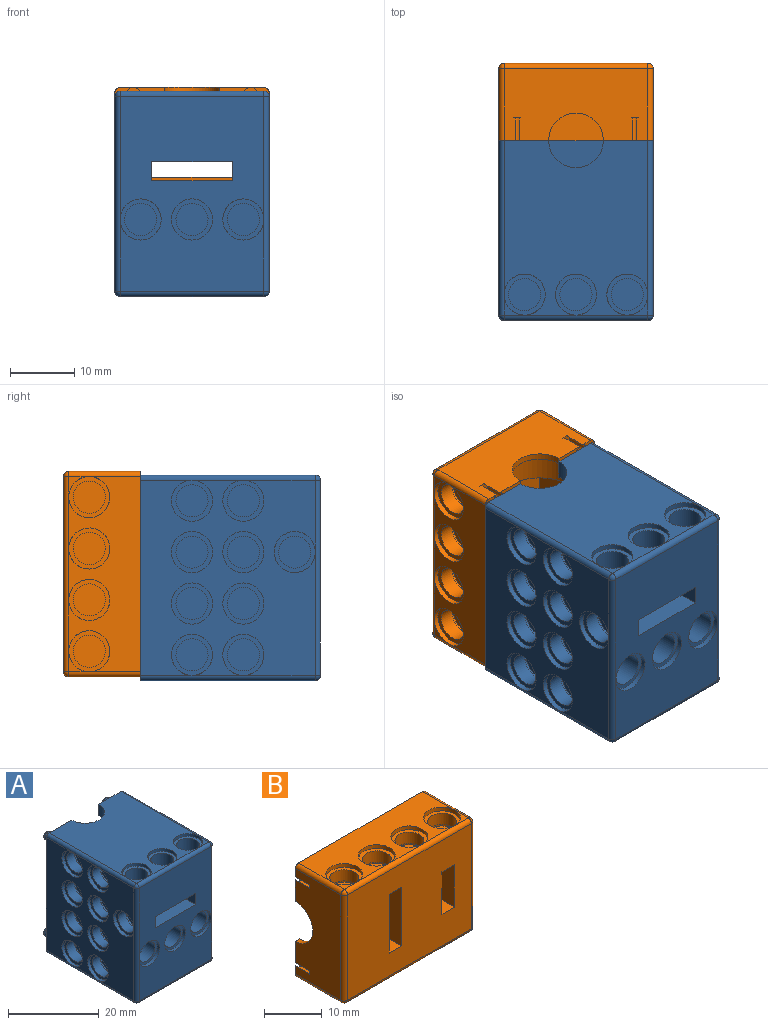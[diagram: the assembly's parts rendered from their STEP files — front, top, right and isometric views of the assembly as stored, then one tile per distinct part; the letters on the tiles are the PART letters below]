
ASSEMBLY  parts=2 mates=1
PART A: 209 faces, bbox 24x31x32 mm
  f0: plane 27.2x22.4mm, normal (0,0,-1), area 508.4mm2, adj f13,f167,f169,f171,f185,f189,f190
  f1: plane 3.2x3.2mm, normal (0,0,-1), area 2.2mm2, adj f171,f189,f190
  f2: plane 27.2x22.4mm, normal (0,0,1), area 480mm2, adj f13,f22,f149,f151,f153,f187,f193,f196
  f3: plane 3.2x3.2mm, normal (0,0,1), area 2.2mm2, adj f149,f193,f196
  f4: plane 3.2x3.2mm, normal (0,0,1), area 2.2mm2, adj f153,f187,f193
  f5: plane 30.4x27.2mm, normal (-1,0,0), area 537.4mm2, adj f13,f23,f25,f27,f29,f31,f33,f35
  f6: plane 3.2x3.2mm, normal (0,0,-1), area 2.2mm2, adj f167,f185,f189
  f7: plane 28x22mm, normal (1,0,0), area 407mm2, adj f8,f10,f12,f13,f14,f15,f16,f17
  f8: plane 12.5x11mm, normal (0,0,-1), area 137.5mm2, adj f7,f9,f12,f15
  f9: plane 28x22mm, normal (-1,0,0), area 407mm2, adj f8,f10,f12,f13,f14,f15,f16,f17
  f10: plane 12.5x11mm, normal (0,0,1), area 137.5mm2, adj f7,f9,f12,f16
  f11: plane 30.4x27.2mm, normal (1,0,0), area 537.4mm2, adj f13,f77,f79,f81,f83,f85,f87,f89
  f12: plane 30.4x22.4mm, normal (0,-1,0), area 547mm2, adj f7,f8,f9,f10,f131,f133,f135,f188
  f13: plane 32x24mm, normal (0,1,0), area 404.4mm2, adj f0,f2,f5,f7,f9,f11,f17,f19
  f14: plane 17x12.5mm, normal (0,0,-1), area 139.5mm2, adj f7,f9,f15,f18,f19,f20
  f15: plane 12.5x4mm, normal (0,1,0), area 50mm2, adj f7,f8,f9,f14
  f16: plane 15x12.5mm, normal (0,1,0), area 187.5mm2, adj f7,f9,f10,f17
  f17: plane 17x12.5mm, normal (0,0,1), area 212.5mm2, adj f7,f9,f13,f16
  f18: cylinder r=2.75mm len=5.5mm, axis (0,0,1), area 37.6mm2, adj f14,f19,f20,f21
  f19: cylinder r=6.25mm len=5.63mm, axis (0,0,1), area 28mm2, adj f13,f14,f18,f21
  f20: cylinder r=6.25mm len=5.63mm, axis (0,0,1), area 28mm2, adj f13,f14,f18,f21
  f21: plane 12.5x8.75mm, normal (0,0,-1), area 44.6mm2, adj f13,f18,f19,f20,f22
  f22: cylinder r=4.25mm len=8.5mm, axis (0,0,1), area 40.1mm2, adj f2,f13,f21
  f23: cylinder r=3.2mm len=6.4mm, axis (-1,0,0), area 16.1mm2, adj f5,f24
  f24: plane 6.4x6.4mm, normal (-1,0,0), area 12.5mm2, adj f23,f44
  f25: cylinder r=3.2mm len=6.4mm, axis (-1,0,0), area 16.1mm2, adj f5,f26
  f26: plane 6.4x6.4mm, normal (-1,0,0), area 12.5mm2, adj f25,f48
  f27: cylinder r=3.2mm len=6.4mm, axis (-1,0,0), area 16.1mm2, adj f5,f28
  f28: plane 6.4x6.4mm, normal (-1,0,0), area 12.5mm2, adj f27,f52
  f29: cylinder r=3.2mm len=6.4mm, axis (-1,0,0), area 16.1mm2, adj f5,f30
  f30: plane 6.4x6.4mm, normal (-1,0,0), area 12.5mm2, adj f29,f56
  f31: cylinder r=3.2mm len=6.4mm, axis (-1,0,0), area 16.1mm2, adj f5,f32
  f32: plane 6.4x6.4mm, normal (-1,0,0), area 12.5mm2, adj f31,f60
  f33: cylinder r=3.2mm len=6.4mm, axis (-1,0,0), area 16.1mm2, adj f5,f34
  f34: plane 6.4x6.4mm, normal (-1,0,0), area 12.5mm2, adj f33,f64
  f35: cylinder r=3.2mm len=6.4mm, axis (-1,0,0), area 16.1mm2, adj f5,f36
  f36: plane 6.4x6.4mm, normal (-1,0,0), area 12.5mm2, adj f35,f68
  f37: cylinder r=3.2mm len=6.4mm, axis (-1,0,0), area 16.1mm2, adj f5,f38
  f38: plane 6.4x6.4mm, normal (-1,0,0), area 12.5mm2, adj f37,f72
  f39: cylinder r=3.2mm len=6.4mm, axis (-1,0,0), area 16.1mm2, adj f5,f40
  f40: plane 6.4x6.4mm, normal (-1,0,0), area 12.5mm2, adj f39,f76
  f41: plane 6.4x6.4mm, normal (-1,0,0), area 32.2mm2, adj f42
  f42: cylinder r=3.2mm len=6.4mm, axis (-1,0,0), area 16.1mm2, adj f41,f43
  f43: plane 6.4x6.4mm, normal (1,0,0), area 12.5mm2, adj f42,f44
  f44: cylinder r=2.5mm len=5mm, axis (-1,0,0), area 37.7mm2, adj f24,f43
  f45: plane 6.4x6.4mm, normal (-1,0,0), area 32.2mm2, adj f46
  f46: cylinder r=3.2mm len=6.4mm, axis (-1,0,0), area 16.1mm2, adj f45,f47
  f47: plane 6.4x6.4mm, normal (1,0,0), area 12.5mm2, adj f46,f48
  f48: cylinder r=2.5mm len=5mm, axis (-1,0,0), area 37.7mm2, adj f26,f47
  f49: plane 6.4x6.4mm, normal (-1,0,0), area 32.2mm2, adj f50
  f50: cylinder r=3.2mm len=6.4mm, axis (-1,0,0), area 16.1mm2, adj f49,f51
  f51: plane 6.4x6.4mm, normal (1,0,0), area 12.5mm2, adj f50,f52
  f52: cylinder r=2.5mm len=5mm, axis (-1,0,0), area 37.7mm2, adj f28,f51
  f53: plane 6.4x6.4mm, normal (-1,0,0), area 32.2mm2, adj f54
  f54: cylinder r=3.2mm len=6.4mm, axis (-1,0,0), area 16.1mm2, adj f53,f55
  f55: plane 6.4x6.4mm, normal (1,0,0), area 12.5mm2, adj f54,f56
  f56: cylinder r=2.5mm len=5mm, axis (-1,0,0), area 37.7mm2, adj f30,f55
  f57: plane 6.4x6.4mm, normal (-1,0,0), area 32.2mm2, adj f58
  f58: cylinder r=3.2mm len=6.4mm, axis (-1,0,0), area 16.1mm2, adj f57,f59
  f59: plane 6.4x6.4mm, normal (1,0,0), area 12.5mm2, adj f58,f60
  f60: cylinder r=2.5mm len=5mm, axis (-1,0,0), area 37.7mm2, adj f32,f59
  f61: plane 6.4x6.4mm, normal (-1,0,0), area 32.2mm2, adj f62
  f62: cylinder r=3.2mm len=6.4mm, axis (-1,0,0), area 16.1mm2, adj f61,f63
  f63: plane 6.4x6.4mm, normal (1,0,0), area 12.5mm2, adj f62,f64
  f64: cylinder r=2.5mm len=5mm, axis (-1,0,0), area 37.7mm2, adj f34,f63
  f65: plane 6.4x6.4mm, normal (-1,0,0), area 32.2mm2, adj f66
  f66: cylinder r=3.2mm len=6.4mm, axis (-1,0,0), area 16.1mm2, adj f65,f67
  f67: plane 6.4x6.4mm, normal (1,0,0), area 12.5mm2, adj f66,f68
  f68: cylinder r=2.5mm len=5mm, axis (-1,0,0), area 37.7mm2, adj f36,f67
  f69: plane 6.4x6.4mm, normal (-1,0,0), area 32.2mm2, adj f70
  f70: cylinder r=3.2mm len=6.4mm, axis (-1,0,0), area 16.1mm2, adj f69,f71
  f71: plane 6.4x6.4mm, normal (1,0,0), area 12.5mm2, adj f70,f72
  f72: cylinder r=2.5mm len=5mm, axis (-1,0,0), area 37.7mm2, adj f38,f71
  f73: plane 6.4x6.4mm, normal (-1,0,0), area 32.2mm2, adj f74
  f74: cylinder r=3.2mm len=6.4mm, axis (-1,0,0), area 16.1mm2, adj f73,f75
  f75: plane 6.4x6.4mm, normal (1,0,0), area 12.5mm2, adj f74,f76
  f76: cylinder r=2.5mm len=5mm, axis (-1,0,0), area 37.7mm2, adj f40,f75
  f77: cylinder r=3.2mm len=6.4mm, axis (1,0,0), area 16.1mm2, adj f11,f78
  f78: plane 6.4x6.4mm, normal (1,0,0), area 12.5mm2, adj f77,f98
  f79: cylinder r=3.2mm len=6.4mm, axis (1,0,0), area 16.1mm2, adj f11,f80
  f80: plane 6.4x6.4mm, normal (1,0,0), area 12.5mm2, adj f79,f102
  f81: cylinder r=3.2mm len=6.4mm, axis (1,0,0), area 16.1mm2, adj f11,f82
  f82: plane 6.4x6.4mm, normal (1,0,0), area 12.5mm2, adj f81,f106
  f83: cylinder r=3.2mm len=6.4mm, axis (1,0,0), area 16.1mm2, adj f11,f84
  f84: plane 6.4x6.4mm, normal (1,0,0), area 12.5mm2, adj f83,f110
  f85: cylinder r=3.2mm len=6.4mm, axis (1,0,0), area 16.1mm2, adj f11,f86
  f86: plane 6.4x6.4mm, normal (1,0,0), area 12.5mm2, adj f85,f114
  f87: cylinder r=3.2mm len=6.4mm, axis (1,0,0), area 16.1mm2, adj f11,f88
  f88: plane 6.4x6.4mm, normal (1,0,0), area 12.5mm2, adj f87,f118
  f89: cylinder r=3.2mm len=6.4mm, axis (1,0,0), area 16.1mm2, adj f11,f90
  f90: plane 6.4x6.4mm, normal (1,0,0), area 12.5mm2, adj f89,f122
  f91: cylinder r=3.2mm len=6.4mm, axis (1,0,0), area 16.1mm2, adj f11,f92
  f92: plane 6.4x6.4mm, normal (1,0,0), area 12.5mm2, adj f91,f126
  f93: cylinder r=3.2mm len=6.4mm, axis (1,0,0), area 16.1mm2, adj f11,f94
  f94: plane 6.4x6.4mm, normal (1,0,0), area 12.5mm2, adj f93,f130
  f95: plane 6.4x6.4mm, normal (1,0,0), area 32.2mm2, adj f96
  f96: cylinder r=3.2mm len=6.4mm, axis (1,0,0), area 16.1mm2, adj f95,f97
  f97: plane 6.4x6.4mm, normal (-1,0,0), area 12.5mm2, adj f96,f98
  f98: cylinder r=2.5mm len=5mm, axis (1,0,0), area 37.7mm2, adj f78,f97
  f99: plane 6.4x6.4mm, normal (1,0,0), area 32.2mm2, adj f100
  f100: cylinder r=3.2mm len=6.4mm, axis (1,0,0), area 16.1mm2, adj f99,f101
  f101: plane 6.4x6.4mm, normal (-1,0,0), area 12.5mm2, adj f100,f102
  f102: cylinder r=2.5mm len=5mm, axis (1,0,0), area 37.7mm2, adj f80,f101
  f103: plane 6.4x6.4mm, normal (1,0,0), area 32.2mm2, adj f104
  f104: cylinder r=3.2mm len=6.4mm, axis (1,0,0), area 16.1mm2, adj f103,f105
  f105: plane 6.4x6.4mm, normal (-1,0,0), area 12.5mm2, adj f104,f106
  f106: cylinder r=2.5mm len=5mm, axis (1,0,0), area 37.7mm2, adj f82,f105
  f107: plane 6.4x6.4mm, normal (1,0,0), area 32.2mm2, adj f108
  f108: cylinder r=3.2mm len=6.4mm, axis (1,0,0), area 16.1mm2, adj f107,f109
  f109: plane 6.4x6.4mm, normal (-1,0,0), area 12.5mm2, adj f108,f110
  f110: cylinder r=2.5mm len=5mm, axis (1,0,0), area 37.7mm2, adj f84,f109
  f111: plane 6.4x6.4mm, normal (1,0,0), area 32.2mm2, adj f112
  f112: cylinder r=3.2mm len=6.4mm, axis (1,0,0), area 16.1mm2, adj f111,f113
  f113: plane 6.4x6.4mm, normal (-1,0,0), area 12.5mm2, adj f112,f114
  f114: cylinder r=2.5mm len=5mm, axis (1,0,0), area 37.7mm2, adj f86,f113
  f115: plane 6.4x6.4mm, normal (1,0,0), area 32.2mm2, adj f116
  f116: cylinder r=3.2mm len=6.4mm, axis (1,0,0), area 16.1mm2, adj f115,f117
  f117: plane 6.4x6.4mm, normal (-1,0,0), area 12.5mm2, adj f116,f118
  f118: cylinder r=2.5mm len=5mm, axis (1,0,0), area 37.7mm2, adj f88,f117
  f119: plane 6.4x6.4mm, normal (1,0,0), area 32.2mm2, adj f120
  f120: cylinder r=3.2mm len=6.4mm, axis (1,0,0), area 16.1mm2, adj f119,f121
  f121: plane 6.4x6.4mm, normal (-1,0,0), area 12.5mm2, adj f120,f122
  f122: cylinder r=2.5mm len=5mm, axis (1,0,0), area 37.7mm2, adj f90,f121
  f123: plane 6.4x6.4mm, normal (1,0,0), area 32.2mm2, adj f124
  f124: cylinder r=3.2mm len=6.4mm, axis (1,0,0), area 16.1mm2, adj f123,f125
  f125: plane 6.4x6.4mm, normal (-1,0,0), area 12.5mm2, adj f124,f126
  f126: cylinder r=2.5mm len=5mm, axis (1,0,0), area 37.7mm2, adj f92,f125
  f127: plane 6.4x6.4mm, normal (1,0,0), area 32.2mm2, adj f128
  f128: cylinder r=3.2mm len=6.4mm, axis (1,0,0), area 16.1mm2, adj f127,f129
  f129: plane 6.4x6.4mm, normal (-1,0,0), area 12.5mm2, adj f128,f130
  f130: cylinder r=2.5mm len=5mm, axis (1,0,0), area 37.7mm2, adj f94,f129
  f131: cylinder r=3.2mm len=6.4mm, axis (0,-1,0), area 16.1mm2, adj f12,f132
  f132: plane 6.4x6.4mm, normal (0,-1,0), area 12.5mm2, adj f131,f140
  f133: cylinder r=3.2mm len=6.4mm, axis (0,-1,0), area 16.1mm2, adj f12,f134
  f134: plane 6.4x6.4mm, normal (0,-1,0), area 12.5mm2, adj f133,f144
  f135: cylinder r=3.2mm len=6.4mm, axis (0,-1,0), area 16.1mm2, adj f12,f136
  f136: plane 6.4x6.4mm, normal (0,-1,0), area 12.5mm2, adj f135,f148
  f137: plane 6.4x6.4mm, normal (0,-1,0), area 32.2mm2, adj f138
  f138: cylinder r=3.2mm len=6.4mm, axis (0,-1,0), area 16.1mm2, adj f137,f139
  f139: plane 6.4x6.4mm, normal (0,1,0), area 12.5mm2, adj f138,f140
  f140: cylinder r=2.5mm len=6.4mm, axis (0,-1,0), area 100.5mm2, adj f132,f139
  f141: plane 6.4x6.4mm, normal (0,-1,0), area 32.2mm2, adj f142
  f142: cylinder r=3.2mm len=6.4mm, axis (0,-1,0), area 16.1mm2, adj f141,f143
  f143: plane 6.4x6.4mm, normal (0,1,0), area 12.5mm2, adj f142,f144
  f144: cylinder r=2.5mm len=6.4mm, axis (0,-1,0), area 100.5mm2, adj f134,f143
  f145: plane 6.4x6.4mm, normal (0,-1,0), area 32.2mm2, adj f146
  f146: cylinder r=3.2mm len=6.4mm, axis (0,-1,0), area 16.1mm2, adj f145,f147
  f147: plane 6.4x6.4mm, normal (0,1,0), area 12.5mm2, adj f146,f148
  f148: cylinder r=2.5mm len=6.4mm, axis (0,-1,0), area 100.5mm2, adj f136,f147
  f149: cylinder r=3.2mm len=6.4mm, axis (0,0,1), area 16.1mm2, adj f2,f3,f150
  f150: plane 6.4x6.4mm, normal (0,0,1), area 12.5mm2, adj f149,f158
  f151: cylinder r=3.2mm len=6.4mm, axis (0,0,1), area 16.1mm2, adj f2,f152
  f152: plane 6.4x6.4mm, normal (0,0,1), area 12.5mm2, adj f151,f162
  f153: cylinder r=3.2mm len=6.4mm, axis (0,0,1), area 16.1mm2, adj f2,f4,f154
  f154: plane 6.4x6.4mm, normal (0,0,1), area 12.5mm2, adj f153,f166
  f155: plane 6.4x6.4mm, normal (0,0,1), area 32.2mm2, adj f156
  f156: cylinder r=3.2mm len=6.4mm, axis (0,0,1), area 16.1mm2, adj f155,f157
  f157: plane 6.4x6.4mm, normal (0,0,-1), area 12.5mm2, adj f156,f158
  f158: cylinder r=2.5mm len=6.4mm, axis (0,0,1), area 100.5mm2, adj f150,f157
  f159: plane 6.4x6.4mm, normal (0,0,1), area 32.2mm2, adj f160
  f160: cylinder r=3.2mm len=6.4mm, axis (0,0,1), area 16.1mm2, adj f159,f161
  f161: plane 6.4x6.4mm, normal (0,0,-1), area 12.5mm2, adj f160,f162
  f162: cylinder r=2.5mm len=6.4mm, axis (0,0,1), area 100.5mm2, adj f152,f161
  f163: plane 6.4x6.4mm, normal (0,0,1), area 32.2mm2, adj f164
  f164: cylinder r=3.2mm len=6.4mm, axis (0,0,1), area 16.1mm2, adj f163,f165
  f165: plane 6.4x6.4mm, normal (0,0,-1), area 12.5mm2, adj f164,f166
  f166: cylinder r=2.5mm len=6.4mm, axis (0,0,1), area 100.5mm2, adj f154,f165
  f167: cylinder r=3.2mm len=6.4mm, axis (0,0,-1), area 16.1mm2, adj f0,f6,f168
  f168: plane 6.4x6.4mm, normal (0,0,-1), area 12.5mm2, adj f167,f176
  f169: cylinder r=3.2mm len=6.4mm, axis (0,0,-1), area 16.1mm2, adj f0,f170
  f170: plane 6.4x6.4mm, normal (0,0,-1), area 12.5mm2, adj f169,f180
  f171: cylinder r=3.2mm len=6.4mm, axis (0,0,-1), area 16.1mm2, adj f0,f1,f172
  f172: plane 6.4x6.4mm, normal (0,0,-1), area 12.5mm2, adj f171,f184
  f173: plane 6.4x6.4mm, normal (0,0,-1), area 32.2mm2, adj f174
  f174: cylinder r=3.2mm len=6.4mm, axis (0,0,-1), area 16.1mm2, adj f173,f175
  f175: plane 6.4x6.4mm, normal (0,0,1), area 12.5mm2, adj f174,f176
  f176: cylinder r=2.5mm len=6.4mm, axis (0,0,-1), area 100.5mm2, adj f168,f175
  f177: plane 6.4x6.4mm, normal (0,0,-1), area 32.2mm2, adj f178
  f178: cylinder r=3.2mm len=6.4mm, axis (0,0,-1), area 16.1mm2, adj f177,f179
  f179: plane 6.4x6.4mm, normal (0,0,1), area 12.5mm2, adj f178,f180
  f180: cylinder r=2.5mm len=6.4mm, axis (0,0,-1), area 100.5mm2, adj f170,f179
  f181: plane 6.4x6.4mm, normal (0,0,-1), area 32.2mm2, adj f182
  f182: cylinder r=3.2mm len=6.4mm, axis (0,0,-1), area 16.1mm2, adj f181,f183
  f183: plane 6.4x6.4mm, normal (0,0,1), area 12.5mm2, adj f182,f184
  f184: cylinder r=2.5mm len=6.4mm, axis (0,0,-1), area 100.5mm2, adj f172,f183
  f185: cylinder r=0.8mm len=27.2mm, axis (0,-1,0), area 34.2mm2, adj f0,f6,f11,f13,f186
  f186: sphere r=0.8mm, area 1mm2, adj f185,f188,f189
  f187: cylinder r=0.8mm len=27.2mm, axis (0,1,0), area 34.2mm2, adj f2,f4,f11,f13,f191
  f188: cylinder r=0.8mm len=30.4mm, axis (0,0,-1), area 38.2mm2, adj f11,f12,f186,f191
  f189: cylinder r=0.8mm len=22.4mm, axis (-1,0,0), area 28.1mm2, adj f0,f1,f6,f12,f186,f192
  f190: cylinder r=0.8mm len=27.2mm, axis (0,1,0), area 34.2mm2, adj f0,f1,f5,f13,f192
  f191: sphere r=0.8mm, area 1mm2, adj f187,f188,f193
  f192: sphere r=0.8mm, area 1mm2, adj f189,f190,f194
  f193: cylinder r=0.8mm len=22.4mm, axis (1,0,0), area 28.1mm2, adj f2,f3,f4,f12,f191,f195
  f194: cylinder r=0.8mm len=30.4mm, axis (0,0,1), area 38.2mm2, adj f5,f12,f192,f195
  f195: sphere r=0.8mm, area 1mm2, adj f193,f194,f196
  f196: cylinder r=0.8mm len=27.2mm, axis (0,-1,0), area 34.2mm2, adj f2,f3,f5,f13,f195
  f197: cylinder r=1mm len=2.5mm, axis (0,-1,0), area 15.7mm2, adj f13,f208
  f198: plane 1x1mm, normal (0,1,0), area 0.8mm2, adj f208
  f199: cylinder r=1mm len=2.5mm, axis (0,-1,0), area 15.7mm2, adj f13,f207
  f200: plane 1x1mm, normal (0,1,0), area 0.8mm2, adj f207
  f201: cylinder r=1mm len=2.5mm, axis (0,-1,0), area 15.7mm2, adj f13,f206
  f202: plane 1x1mm, normal (0,1,0), area 0.8mm2, adj f206
  f203: cylinder r=1mm len=2.5mm, axis (0,-1,0), area 15.7mm2, adj f13,f205
  f204: plane 1x1mm, normal (0,1,0), area 0.8mm2, adj f205
  f205: torus R=0.5mm, axis (0,1,0), area 4mm2, adj f203,f204
  f206: torus R=0.5mm, axis (0,1,0), area 4mm2, adj f201,f202
  f207: torus R=0.5mm, axis (0,1,0), area 4mm2, adj f199,f200
  f208: torus R=0.5mm, axis (0,1,0), area 4mm2, adj f197,f198
PART B: 95 faces, bbox 32x12x24 mm
  f0: plane 32x24mm, normal (0,1,0), area 402.6mm2, adj f1,f3,f9,f12,f15,f16,f17,f19
  f1: plane 30.4x11.2mm, normal (0,0,-1), area 207.4mm2, adj f0,f50,f52,f54,f56,f74,f78,f79
  f2: plane 3.2x3.2mm, normal (0,0,-1), area 2.2mm2, adj f50,f78,f79
  f3: plane 30.4x11.2mm, normal (0,0,1), area 207.4mm2, adj f0,f26,f28,f30,f32,f76,f82,f85
  f4: plane 3.2x3.2mm, normal (0,0,1), area 2.2mm2, adj f32,f82,f85
  f5: plane 12.5x5.75mm, normal (1,0,0), area 71.9mm2, adj f15,f16,f18,f23
  f6: plane 12.5x5.75mm, normal (-1,0,0), area 71.9mm2, adj f15,f16,f18,f22
  f7: plane 9x5.75mm, normal (1,0,0), area 51.8mm2, adj f10,f11,f18,f22
  f8: plane 9x3.75mm, normal (-1,0,0), area 33.8mm2, adj f10,f11,f18,f86
  f9: cylinder r=6.25mm len=12.5mm, axis (-1,0,0), area 98.2mm2, adj f0,f19,f24,f25
  f10: plane 5.75x4.4mm, normal (0,0,-1), area 19.1mm2, adj f7,f8,f18,f20,f22,f86
  f11: plane 5.75x4.4mm, normal (0,0,1), area 19.1mm2, adj f7,f8,f18,f20,f22,f86
  f12: plane 22.4x11.2mm, normal (-1,0,0), area 218mm2, adj f0,f21,f79,f83,f85,f91,f92,f93
  f13: plane 3.2x3.2mm, normal (0,0,1), area 2.2mm2, adj f26,f76,f82
  f14: plane 3.2x3.2mm, normal (0,0,-1), area 2.2mm2, adj f56,f74,f78
  f15: plane 22.4x12mm, normal (0,0,-1), area 157.2mm2, adj f0,f5,f6,f18,f20,f22,f23,f25
  f16: plane 22.4x12mm, normal (0,0,1), area 157.2mm2, adj f0,f5,f6,f18,f20,f22,f23,f24
  f17: plane 22.4x11.2mm, normal (1,0,0), area 250.9mm2, adj f0,f74,f76,f77
  f18: plane 30.4x22.4mm, normal (0,-1,0), area 616.5mm2, adj f5,f6,f7,f8,f10,f11,f15,f16
  f19: plane 12.5x6.25mm, normal (1,0,0), area 33mm2, adj f0,f9,f21
  f20: plane 12.5x6.85mm, normal (-1,0,0), area 83.5mm2, adj f0,f10,f11,f15,f16,f22,f86
  f21: cylinder r=4.25mm len=8.5mm, axis (-1,0,0), area 13.4mm2, adj f0,f12,f19
  f22: plane 14.4x12.5mm, normal (0,1,0), area 140.4mm2, adj f6,f7,f10,f11,f15,f16,f20
  f23: plane 12.5x5mm, normal (0,1,0), area 62.5mm2, adj f5,f15,f16,f24,f25
  f24: plane 6.25x6.25mm, normal (1,0,0), area 8.4mm2, adj f9,f16,f23
  f25: plane 6.25x6.25mm, normal (1,0,0), area 8.4mm2, adj f9,f15,f23
  f26: cylinder r=3.2mm len=6.4mm, axis (0,0,1), area 16.1mm2, adj f3,f13,f27
  f27: plane 6.4x6.4mm, normal (0,0,1), area 12.5mm2, adj f26,f34
  f28: cylinder r=3.2mm len=6.4mm, axis (0,0,1), area 16.1mm2, adj f3,f29
  f29: plane 6.4x6.4mm, normal (0,0,1), area 12.5mm2, adj f28,f35
  f30: cylinder r=3.2mm len=6.4mm, axis (0,0,1), area 16.1mm2, adj f3,f31
  f31: plane 6.4x6.4mm, normal (0,0,1), area 12.5mm2, adj f30,f36
  f32: cylinder r=3.2mm len=6.4mm, axis (0,0,1), area 16.1mm2, adj f3,f4,f33
  f33: plane 6.4x6.4mm, normal (0,0,1), area 12.5mm2, adj f32,f37
  f34: cylinder r=2.5mm len=5mm, axis (0,0,1), area 37.7mm2, adj f27,f48
  f35: cylinder r=2.5mm len=5mm, axis (0,0,1), area 37.7mm2, adj f29,f45
  f36: cylinder r=2.5mm len=5mm, axis (0,0,1), area 37.7mm2, adj f31,f42
  f37: cylinder r=2.5mm len=5mm, axis (0,0,1), area 37.7mm2, adj f33,f39
  f38: cylinder r=3.2mm len=6.4mm, axis (0,0,1), area 16.1mm2, adj f39,f40
  f39: plane 6.4x6.4mm, normal (0,0,-1), area 12.5mm2, adj f37,f38
  f40: plane 6.4x6.4mm, normal (0,0,1), area 32.2mm2, adj f38
  f41: cylinder r=3.2mm len=6.4mm, axis (0,0,1), area 16.1mm2, adj f42,f43
  f42: plane 6.4x6.4mm, normal (0,0,-1), area 12.5mm2, adj f36,f41
  f43: plane 6.4x6.4mm, normal (0,0,1), area 32.2mm2, adj f41
  f44: cylinder r=3.2mm len=6.4mm, axis (0,0,1), area 16.1mm2, adj f45,f46
  f45: plane 6.4x6.4mm, normal (0,0,-1), area 12.5mm2, adj f35,f44
  f46: plane 6.4x6.4mm, normal (0,0,1), area 32.2mm2, adj f44
  f47: cylinder r=3.2mm len=6.4mm, axis (0,0,1), area 16.1mm2, adj f48,f49
  f48: plane 6.4x6.4mm, normal (0,0,-1), area 12.5mm2, adj f34,f47
  f49: plane 6.4x6.4mm, normal (0,0,1), area 32.2mm2, adj f47
  f50: cylinder r=3.2mm len=6.4mm, axis (0,0,-1), area 16.1mm2, adj f1,f2,f51
  f51: plane 6.4x6.4mm, normal (0,0,-1), area 12.5mm2, adj f50,f61
  f52: cylinder r=3.2mm len=6.4mm, axis (0,0,-1), area 16.1mm2, adj f1,f53
  f53: plane 6.4x6.4mm, normal (0,0,-1), area 12.5mm2, adj f52,f65
  f54: cylinder r=3.2mm len=6.4mm, axis (0,0,-1), area 16.1mm2, adj f1,f55
  f55: plane 6.4x6.4mm, normal (0,0,-1), area 12.5mm2, adj f54,f69
  f56: cylinder r=3.2mm len=6.4mm, axis (0,0,-1), area 16.1mm2, adj f1,f14,f57
  f57: plane 6.4x6.4mm, normal (0,0,-1), area 12.5mm2, adj f56,f73
  f58: plane 6.4x6.4mm, normal (0,0,-1), area 32.2mm2, adj f59
  f59: cylinder r=3.2mm len=6.4mm, axis (0,0,-1), area 16.1mm2, adj f58,f60
  f60: plane 6.4x6.4mm, normal (0,0,1), area 12.5mm2, adj f59,f61
  f61: cylinder r=2.5mm len=5mm, axis (0,0,-1), area 37.7mm2, adj f51,f60
  f62: plane 6.4x6.4mm, normal (0,0,-1), area 32.2mm2, adj f63
  f63: cylinder r=3.2mm len=6.4mm, axis (0,0,-1), area 16.1mm2, adj f62,f64
  f64: plane 6.4x6.4mm, normal (0,0,1), area 12.5mm2, adj f63,f65
  f65: cylinder r=2.5mm len=5mm, axis (0,0,-1), area 37.7mm2, adj f53,f64
  f66: plane 6.4x6.4mm, normal (0,0,-1), area 32.2mm2, adj f67
  f67: cylinder r=3.2mm len=6.4mm, axis (0,0,-1), area 16.1mm2, adj f66,f68
  f68: plane 6.4x6.4mm, normal (0,0,1), area 12.5mm2, adj f67,f69
  f69: cylinder r=2.5mm len=5mm, axis (0,0,-1), area 37.7mm2, adj f55,f68
  f70: plane 6.4x6.4mm, normal (0,0,-1), area 32.2mm2, adj f71
  f71: cylinder r=3.2mm len=6.4mm, axis (0,0,-1), area 16.1mm2, adj f70,f72
  f72: plane 6.4x6.4mm, normal (0,0,1), area 12.5mm2, adj f71,f73
  f73: cylinder r=2.5mm len=5mm, axis (0,0,-1), area 37.7mm2, adj f57,f72
  f74: cylinder r=0.8mm len=11.2mm, axis (0,-1,0), area 14.1mm2, adj f0,f1,f14,f17,f75
  f75: sphere r=0.8mm, area 1mm2, adj f74,f77,f78
  f76: cylinder r=0.8mm len=11.2mm, axis (0,1,0), area 14.1mm2, adj f0,f3,f13,f17,f80
  f77: cylinder r=0.8mm len=22.4mm, axis (0,0,-1), area 28.1mm2, adj f17,f18,f75,f80
  f78: cylinder r=0.8mm len=30.4mm, axis (-1,0,0), area 38.2mm2, adj f1,f2,f14,f18,f75,f81
  f79: cylinder r=0.8mm len=11.2mm, axis (0,1,0), area 14.1mm2, adj f0,f1,f2,f12,f81
  f80: sphere r=0.8mm, area 1mm2, adj f76,f77,f82
  f81: sphere r=0.8mm, area 1mm2, adj f78,f79,f83
  f82: cylinder r=0.8mm len=30.4mm, axis (1,0,0), area 38.2mm2, adj f3,f4,f13,f18,f80,f84
  f83: cylinder r=0.8mm len=22.4mm, axis (0,0,1), area 28.1mm2, adj f12,f18,f81,f84
  f84: sphere r=0.8mm, area 1mm2, adj f82,f83,f85
  f85: cylinder r=0.8mm len=11.2mm, axis (0,-1,0), area 14.1mm2, adj f0,f3,f4,f12,f84
  f86: plane 9x1.4mm, normal (-0.71,0.71,0), area 17.8mm2, adj f8,f10,f11,f20
  f87: cylinder r=1.05mm len=3.5mm, axis (0,1,0), area 23.1mm2, adj f0,f88
  f88: plane 2.1x2.1mm, normal (0,1,0), area 3.5mm2, adj f87
  f89: cylinder r=1.05mm len=3.5mm, axis (0,1,0), area 23.1mm2, adj f0,f90
  f90: plane 2.1x2.1mm, normal (0,1,0), area 3.5mm2, adj f89
  f91: plane 2.1x2.05mm, normal (0,1,0), area 3.4mm2, adj f12,f92
  f92: cylinder r=1.05mm len=3.5mm, axis (0,1,0), area 20.8mm2, adj f0,f12,f91
  f93: plane 2.1x2.05mm, normal (0,1,0), area 3.4mm2, adj f12,f94
  f94: cylinder r=1.05mm len=3.5mm, axis (0,1,0), area 20.8mm2, adj f0,f12,f93
PLACE A t=(-57.15,-9.19,20.4)mm
PLACE B rot(axis=(-0.71,0,0.71),180deg) t=(-57.15,-9.19,21.96)mm
MATE fastened B.f0 <-> A.f13  axis (0,-1,0) through (-57.15,-9.19,15.49)mm
